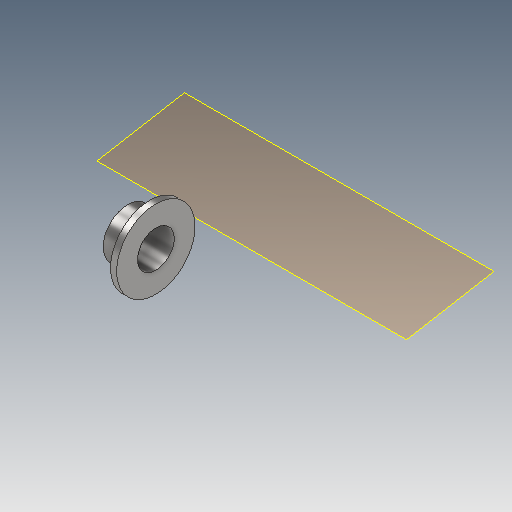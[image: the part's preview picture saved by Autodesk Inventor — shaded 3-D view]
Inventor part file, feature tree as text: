
AUTODESK INVENTOR PART (.ipt)
format: ipt  version: 2025 (Build 290162000, 162)  size: 111,104 bytes
history: native  units: mm
features: other x8, reference x5, plane x1, revolve x1, sketch x1
ambient origin geometry x8: Origin, YZ Plane, XZ Plane, XY Plane, X Axis, Y Axis, Z Axis, Center Point
bodies: 实体1 (feature_tree)
feature tree (16):
  plane  "工作平面1"
  revolve  "旋转1"  Angle=360.0deg
  sketch  "草图1"  dims[d0=20.0mm d1=360.0deg d2=5.0mm d3=12.0mm]
  reference  "参考1"
  reference  "参考2"
  reference  "参考3"
  reference  "参考4"
  reference  "参考5"
  other  "齿轮箱.iam"
  other  "中间轴:1"
  other  "轴承:1"
  other  "滚动轴承 GB/T 276-1994 60000 和 160000 型 6306:1"
  other  "轴:1"
  other  "低速齿轮:1"
  other  "正齿轮:1"
  other  "正齿轮1:1"
